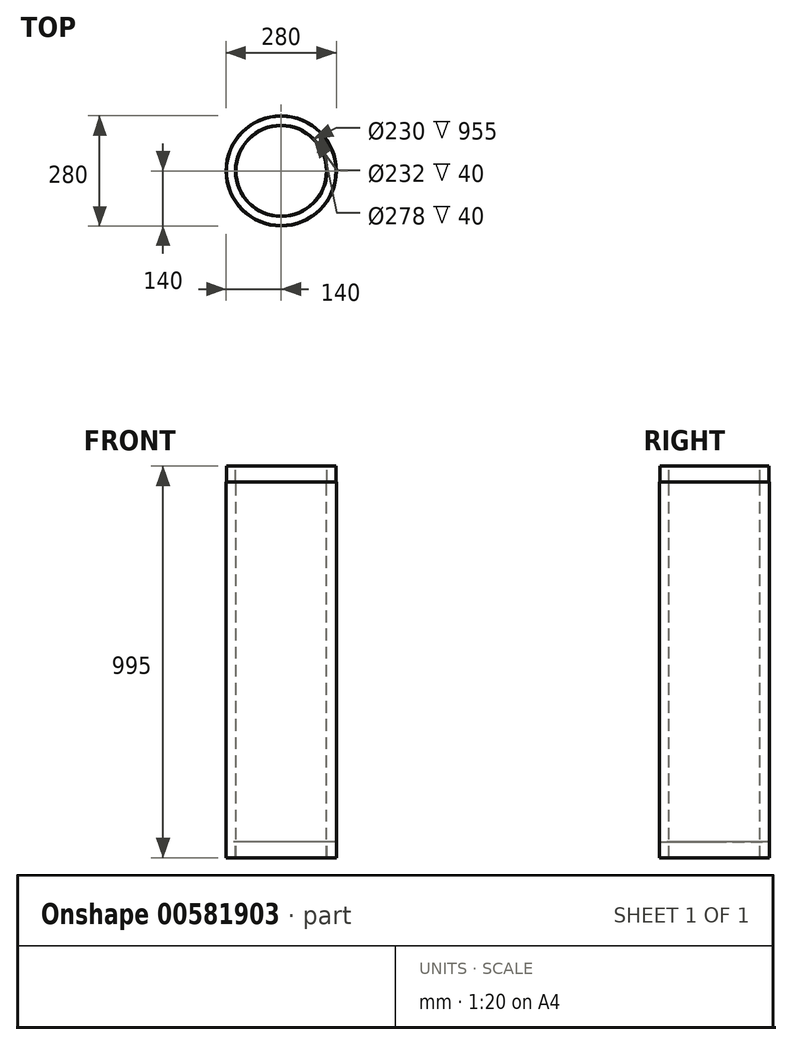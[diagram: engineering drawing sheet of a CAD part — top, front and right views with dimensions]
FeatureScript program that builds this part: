
annotation { "Feature Type Name" : "Feature", "Feature Type Description" : "" }
export const myFeature = defineFeature(function(context is Context, id is Id, definition is map)
    precondition{}
    {
        {
            var Q0;
            Q0=qCreatedBy(makeId("Front.planeOp"),FACE);
            var sketch = newSketch(context, id + "F0", { "sketchPlane" : qUnion([Q0])});
            skLineSegment(sketch, "E0", {"start": v(0, 345.75) * mm, "end": v(0, -558.03) * mm, "construction": true});
            skLineSegment(sketch, "E1", {"start": v(-115, -518.84) * mm, "end": v(-115, 436.16) * mm});
            skLineSegment(sketch, "E2", {"start": v(-115, 436.16) * mm, "end": v(-116, 436.16) * mm});
            skLineSegment(sketch, "E3", {"start": v(-116, 436.16) * mm, "end": v(-116, 476.16) * mm});
            skLineSegment(sketch, "E4", {"start": v(-116, 476.16) * mm, "end": v(-139, 476.16) * mm});
            skLineSegment(sketch, "E5", {"start": v(-139, 476.16) * mm, "end": v(-139, 436.16) * mm});
            skLineSegment(sketch, "E6", {"start": v(-139, 436.16) * mm, "end": v(-140, 436.16) * mm});
            skLineSegment(sketch, "E7", {"start": v(-140, 436.16) * mm, "end": v(-140, -518.84) * mm});
            skLineSegment(sketch, "E8", {"start": v(-140, -518.84) * mm, "end": v(-139, -518.84) * mm});
            skLineSegment(sketch, "E9", {"start": v(-139, -518.84) * mm, "end": v(-139, -478.84) * mm});
            skLineSegment(sketch, "E10", {"start": v(-139, -478.84) * mm, "end": v(-116, -478.84) * mm});
            skLineSegment(sketch, "E11", {"start": v(-116, -478.84) * mm, "end": v(-116, -518.84) * mm});
            skLineSegment(sketch, "E12", {"start": v(-116, -518.84) * mm, "end": v(-115, -518.84) * mm});
            skSolve(sketch);
        }
        {
            var Q0;
            Q0=qSketchRegion(id+"F0",true);
            var Q1;
            Q1=sQuery(id+"F0.wireOp",EDGE,"E0");
            revolve(context, id + "F1", {"entities" : qUnion([Q0]), "axis" : qUnion([Q1]), "revolveType" : RevolveType.FULL});
        }
    });
